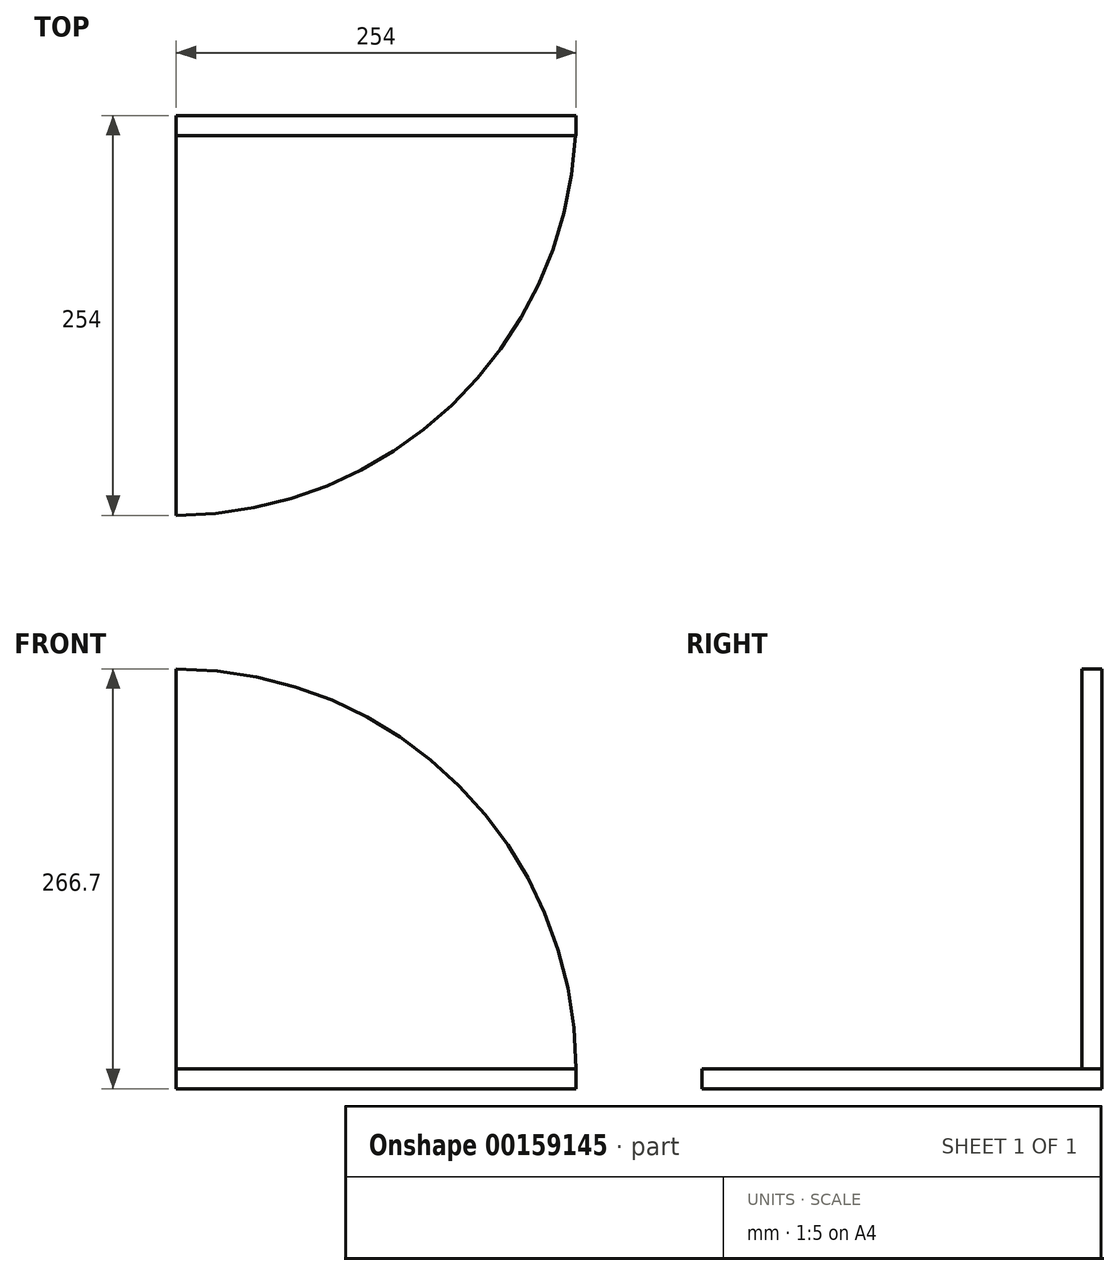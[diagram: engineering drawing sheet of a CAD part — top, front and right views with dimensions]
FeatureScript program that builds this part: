
annotation { "Feature Type Name" : "Feature", "Feature Type Description" : "" }
export const myFeature = defineFeature(function(context is Context, id is Id, definition is map)
    precondition{}
    {
        {
            var Q0;
            Q0=qCreatedBy(makeId("Top.planeOp"),FACE);
            var sketch = newSketch(context, id + "F0", { "sketchPlane" : qUnion([Q0])});
            skLineSegment(sketch, "E0", {"start": v(0, 0) * mm, "end": v(0, -254) * mm});
            skLineSegment(sketch, "E1", {"start": v(0, 0) * mm, "end": v(254, 0) * mm});
            skArc(sketch, "E2", {"start": v(0, -254) * mm, "mid": v(179.6, -179.6) * mm, "end": v(254, 0) * mm});
            skSolve(sketch);
        }
        {
            var Q0;
            Q0 = qSketchRegion(id + "F0", true);
            extrude(context, id + "F1", {"entities" : qUnion([Q0]), "oppositeDirection" : true, "depth" : 12.7 * mm});
        }
        {
            var Q0;
            Q0=qCreatedBy(makeId("Front.planeOp"),FACE);
            var sketch = newSketch(context, id + "F2", { "sketchPlane" : qUnion([Q0])});
            skLineSegment(sketch, "E3", {"start": v(0, 0) * mm, "end": v(0, 254) * mm});
            skLineSegment(sketch, "E4", {"start": v(0, 0) * mm, "end": v(254, 0) * mm});
            skArc(sketch, "E5", {"start": v(254, 0) * mm, "mid": v(179.6, 179.6) * mm, "end": v(0, 254) * mm});
            skSolve(sketch);
        }
        {
            var Q0;
            Q0 = qSketchRegion(id + "F2", true);
            extrude(context, id + "F3", {"entities" : qUnion([Q0]), "depth" : 12.7 * mm});
        }
    });
